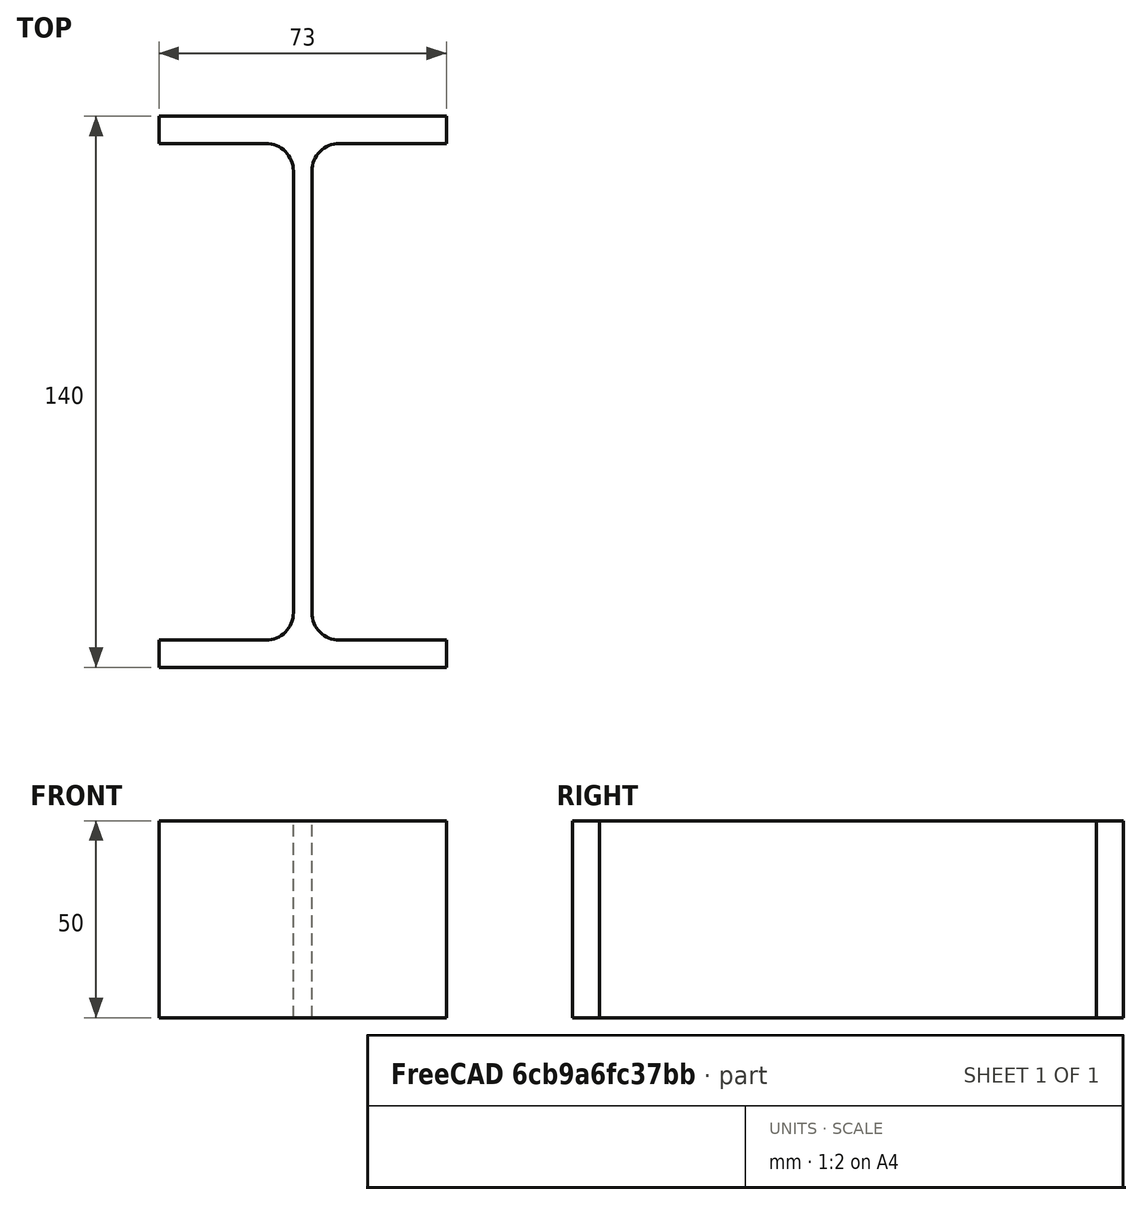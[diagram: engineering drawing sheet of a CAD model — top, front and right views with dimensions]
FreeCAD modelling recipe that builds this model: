
FCSTD DOCUMENT  (FreeCAD 0.15R4671 (Git))
Label: IPE-Profile 140 DIN1025-5 S235JR
License: All rights reserved
LicenseURL: http://en.wikipedia.org/wiki/All_rights_reserved
objects: Sketcher::SketchObject×1, Part::Extrusion×1
note: 2 computed .brp shape members not serialized (recipe doc carries the construction recipe); baked Part::Feature solids carry a one-line shape summary decoded from their .brp

FEATURE [Sketcher::SketchObject] Sketch
  sketch-geometry (16):
    g0: LineSegment StartX=2.35 StartY=-56.1 StartZ=0 EndX=2.35 EndY=56.1 EndZ=0
    g1: LineSegment StartX=9.35 StartY=63.1 StartZ=0 EndX=36.5 EndY=63.1 EndZ=0
    g2: LineSegment StartX=36.5 StartY=63.1 StartZ=0 EndX=36.5 EndY=70 EndZ=0
    g3: LineSegment StartX=36.5 StartY=70 StartZ=0 EndX=-36.5 EndY=70 EndZ=0
    g4: LineSegment StartX=-36.5 StartY=70 StartZ=0 EndX=-36.5 EndY=63.1 EndZ=0
    g5: LineSegment StartX=-36.5 StartY=63.1 StartZ=0 EndX=-9.35 EndY=63.1 EndZ=0
    g6: LineSegment StartX=-2.35 StartY=56.1 StartZ=0 EndX=-2.35 EndY=-56.1 EndZ=0
    g7: LineSegment StartX=-9.35 StartY=-63.1 StartZ=0 EndX=-36.5 EndY=-63.1 EndZ=0
    g8: LineSegment StartX=-36.5 StartY=-63.1 StartZ=0 EndX=-36.5 EndY=-70 EndZ=0
    g9: LineSegment StartX=-36.5 StartY=-70 StartZ=0 EndX=36.5 EndY=-70 EndZ=0
    g10: LineSegment StartX=36.5 StartY=-70 StartZ=0 EndX=36.5 EndY=-63.1 EndZ=0
    g11: LineSegment StartX=36.5 StartY=-63.1 StartZ=0 EndX=9.35 EndY=-63.1 EndZ=0
    g12: ArcOfCircle CenterX=9.35 CenterY=56.1 CenterZ=0 NormalX=0 NormalY=0 NormalZ=1 Radius=7 StartAngle=1.5708 EndAngle=3.14159
    g13: ArcOfCircle CenterX=9.35 CenterY=-56.1 CenterZ=0 NormalX=0 NormalY=0 NormalZ=1 Radius=7 StartAngle=3.14159 EndAngle=4.71239
    g14: ArcOfCircle CenterX=-9.35 CenterY=56.1 CenterZ=0 NormalX=0 NormalY=0 NormalZ=1 Radius=7 StartAngle=0 EndAngle=1.5708
    g15: ArcOfCircle CenterX=-9.35 CenterY=-56.1 CenterZ=0 NormalX=0 NormalY=0 NormalZ=1 Radius=7 StartAngle=4.71239 EndAngle=6.28319
  constraints (42):
    c: Vertical(g0)
    c: Coincident(g2,g1)
    c: Vertical(g2)
    c: Coincident(g3,g2)
    c: Coincident(g4,g3)
    c: Vertical(g4)
    c: Coincident(g5,g4)
    c: Horizontal(g5)
    c: Vertical(g6)
    c: Horizontal(g7)
    c: Coincident(g8,g7)
    c: Vertical(g8)
    c: Coincident(g9,g8)
    c: Horizontal(g9)
    c: Coincident(g10,g9)
    c: Vertical(g10)
    c: Coincident(g11,g10)
    c: Horizontal(g11)
    c: Tangent(g1,g12) = 1.5708
    c: Tangent(g0,g12) = 1.5708
    c: Tangent(g0,g13) = 1.5708
    c: Tangent(g11,g13) = 1.5708
    c: Tangent(g5,g14) = 1.5708
    c: Tangent(g6,g14) = 1.5708
    c: Tangent(g6,g15) = 1.5708
    c: Tangent(g7,g15) = 1.5708
    c: Equal(g3,g9)
    c: Equal(g2,g4)
    c: Equal(g4,g8)
    c: Equal(g8,g10)
    c: Equal(g12,g14)
    c: Equal(g14,g15)
    c: Equal(g15,g13)
    c: Symmetric(g2,g3,g-2)
    c: Symmetric(g9,g8,g-2)
    c: Symmetric(g0,g6,g-2)
    c: Symmetric(g2,g9,g-1)
    c: DistanceY(g2,g9) = -140
    c: DistanceX(g3) = -73
    c: DistanceX(g0,g6) = -4.7
    c: DistanceY(g2) = 6.9
    c: Radius(g12) = 7
FEATURE [Part::Extrusion] Extrude  label="IPE-Profile 140 DIN1025-5 S235JR"
  Base = -> Sketch
  Dir = (0,0,50)
  Solid = true
